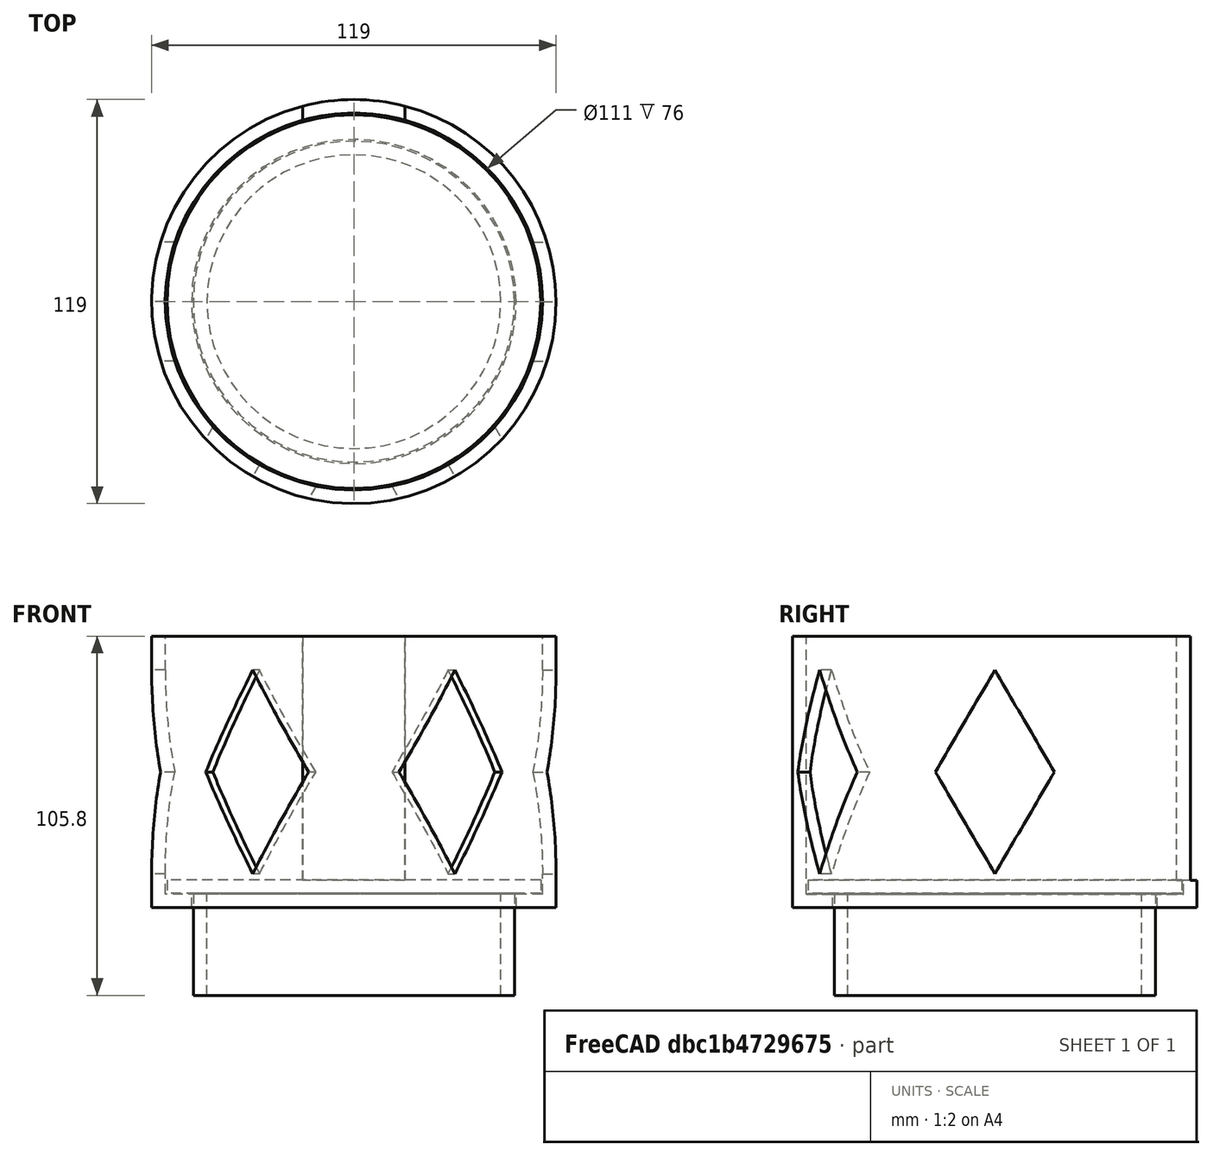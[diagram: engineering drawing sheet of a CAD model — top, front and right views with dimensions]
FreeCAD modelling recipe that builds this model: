
FCSTD DOCUMENT  (FreeCAD 0.19R14555 (Git shallow))
Label: mug_holder
License: All rights reserved
LicenseURL: http://en.wikipedia.org/wiki/All_rights_reserved
objects: Sketcher::SketchObject×4, PartDesign::Revolution×2, PartDesign::Body×2, PartDesign::Pocket×2, Mesh::Feature×2, PartDesign::PolarPattern×1
note: 15 computed .brp shape members not serialized (recipe doc carries the construction recipe); baked Part::Feature solids carry a one-line shape summary decoded from their .brp

FEATURE [Sketcher::SketchObject] Sketch004  label="BottomSketch"
  FullyConstrained = true
  MapMode = 5
  Placement = pos=(0,0,0) rot=(1,0,0;1.5708rad)
  Support = -> [XZ_Plane]
  sketch-geometry (8):
    g0: LineSegment StartX=0 StartY=30 StartZ=0 EndX=0 EndY=34 EndZ=0
    g1: LineSegment StartX=0 StartY=34 StartZ=0 EndX=55 EndY=34 EndZ=0
    g2: LineSegment StartX=55 StartY=34 StartZ=0 EndX=55 EndY=30 EndZ=0
    g3: LineSegment StartX=55 StartY=30 StartZ=0 EndX=47.25 EndY=30 EndZ=0
    g4: LineSegment StartX=47.25 StartY=30 StartZ=0 EndX=47.25 EndY=0 EndZ=0
    g5: LineSegment StartX=47.25 StartY=0 StartZ=0 EndX=43.25 EndY=0 EndZ=0
    g6: LineSegment StartX=43.25 StartY=0 StartZ=0 EndX=43.25 EndY=30 EndZ=0
    g7: LineSegment StartX=43.25 StartY=30 StartZ=0 EndX=0 EndY=30 EndZ=0
  constraints (24):
    c: Coincident(g0,g1)
    c: Coincident(g1,g2)
    c: Coincident(g2,g3)
    c: Coincident(g3,g4)
    c: Coincident(g4,g5)
    c: Coincident(g5,g6)
    c: Coincident(g6,g7)
    c: Coincident(g7,g0)
    c: Horizontal(g1)
    c: Horizontal(g7)
    c: Horizontal(g3)
    c: Horizontal(g5)
    c: Vertical(g0)
    c: Vertical(g2)
    c: Vertical(g4)
    c: Vertical(g6)
    c: DistanceX(g5,g4) = 4
    c: DistanceY(g2,g1) = 4
    c: DistanceX(g-1,g4) = 47.25  'ChairInsetOuterRadius'
    c: Equal(g0,g2)
    c: DistanceY(g4,g3) = 30  'ChairInsetHeight'
    c: PointOnObject(g5,g-1)
    c: PointOnObject(g0,g-2)
    c: DistanceX(g1,g1) = 55  'CupFaceOuterRadius'
FEATURE [PartDesign::Revolution] Revolution  label="BottomRevolution"
  Angle = 360
  Axis = (0,2e-16,1)
  Base = (0,0,0)
  Placement = pos=(0,0,0) rot=(1,0,0;1.5708rad)
  Profile = -> Sketch004
  ReferenceAxis = -> Sketch004 [V_Axis]
  Reversed = true
FEATURE [PartDesign::Body] Body  label="Bottom"
  Group = -> [Sketch004,Revolution]
  Origin = -> Origin
  Tip = -> Revolution
FEATURE [Sketcher::SketchObject] Sketch
  FullyConstrained = true
  MapMode = 5
  Placement = pos=(0,0,0) rot=(1,0,0;1.5708rad)
  Support = -> [XZ_Plane001]
  expr: Constraints[17] = <<BottomSketch>>.Constraints.ChairInsetHeight - 0.2mm
  expr: Constraints[13] = <<BottomSketch>>.Constraints.ChairInsetOuterRadius + 0.5mm
  expr: Constraints[12] = <<BottomSketch>>.Constraints.CupFaceOuterRadius + 0.5mm
  sketch-geometry (6):
    g0: LineSegment StartX=47.75 StartY=29.8 StartZ=0 EndX=55.5 EndY=29.8 EndZ=0
    g1: LineSegment StartX=55.5 StartY=29.8 StartZ=0 EndX=55.5 EndY=105.8 EndZ=0
    g2: LineSegment StartX=55.5 StartY=105.8 StartZ=0 EndX=59.5 EndY=105.8 EndZ=0
    g3: LineSegment StartX=59.5 StartY=105.8 StartZ=0 EndX=59.5 EndY=25.8 EndZ=0
    g4: LineSegment StartX=59.5 StartY=25.8 StartZ=0 EndX=47.75 EndY=25.8 EndZ=0
    g5: LineSegment StartX=47.75 StartY=25.8 StartZ=0 EndX=47.75 EndY=29.8 EndZ=0
  constraints (18):
    c: Horizontal(g0)
    c: Coincident(g0,g1)
    c: Vertical(g1)
    c: Coincident(g1,g2)
    c: Horizontal(g2)
    c: Coincident(g2,g3)
    c: Vertical(g3)
    c: Coincident(g3,g4)
    c: Horizontal(g4)
    c: Coincident(g4,g5)
    c: Coincident(g5,g0)
    c: Vertical(g5)
    c: DistanceX(g-1,g0) = 55.5
    c: DistanceX(g-1,g4) = 47.75
    c: DistanceX(g1,g2) = 4
    c: DistanceY(g4,g0) = 4
    c: DistanceY(g3,g3) = 80
    c: DistanceY(g-1,g0) = 29.8
FEATURE [PartDesign::Revolution] Revolution001
  Angle = 360
  Axis = (0,2e-16,1)
  Base = (0,0,0)
  Placement = pos=(0,0,0) rot=(1,0,0;1.5708rad)
  Profile = -> Sketch
  ReferenceAxis = -> Sketch [V_Axis]
FEATURE [Sketcher::SketchObject] Sketch005
  ExternalGeometry = -> [Revolution001]
  FullyConstrained = true
  MapMode = 5
  Placement = pos=(0,0,0) rot=(0.57735,0.57735,0.57735;2.0944rad)
  Support = -> [YZ_Plane001]
  sketch-geometry (9):
    g0: LineSegment StartX=2.91e-14 StartY=35.8 StartZ=0 EndX=-17.5 EndY=65.8 EndZ=0
    g1: LineSegment StartX=-17.5 StartY=65.8 StartZ=0 EndX=2.84e-14 EndY=95.8 EndZ=0
    g2: LineSegment StartX=2.91e-14 StartY=95.8 StartZ=0 EndX=17.5 EndY=65.8 EndZ=0
    g3: LineSegment StartX=17.5 StartY=65.8 StartZ=0 EndX=2.84e-14 EndY=35.8 EndZ=0
    g4: LineSegment StartX=2.91e-14 StartY=95.8 StartZ=0 EndX=2.91e-14 EndY=35.8 EndZ=0
    g5: LineSegment StartX=-17.5 StartY=65.8 StartZ=0 EndX=17.5 EndY=65.8 EndZ=0
    g6: LineSegment StartX=59.5 StartY=105.8 StartZ=0 EndX=-59.5 EndY=25.8 EndZ=0
    g7: GeomPoint X=2.85e-14 Y=65.8 Z=0
    g8: GeomPoint X=2.85e-14 Y=65.8 Z=0
  constraints (19):
    c: Coincident(g0,g1)
    c: Coincident(g1,g2)
    c: Coincident(g2,g3)
    c: Coincident(g3,g0)
    c: Coincident(g4,g1)
    c: Coincident(g4,g0)
    c: Vertical(g4)
    c: Coincident(g5,g0)
    c: Coincident(g5,g2)
    c: Horizontal(g5)
    c: Equal(g0,g1)
    c: Equal(g1,g2)
    c: Coincident(g6,g-4)
    c: Coincident(g6,g-3)
    c: Symmetric(g6,g6,g7)
    c: Symmetric(g0,g2,g8)
    c: Coincident(g7,g8)
    c: DistanceY(g0,g1) = 60
    c: DistanceX(g0,g2) = 35
FEATURE [PartDesign::Pocket] Pocket
  BaseFeature = -> Revolution001
  Length = 5
  Length2 = 100
  Placement = pos=(0,0,0) rot=(1,0,0;1.5708rad)
  Profile = -> Sketch005
  Type = 1
FEATURE [PartDesign::PolarPattern] PolarPattern
  Angle = 180
  Axis = -> Sketch005 [V_Axis]
  BaseFeature = -> Pocket
  Occurrences = 4
  Originals = -> [Pocket]
  Placement = pos=(0,0,0) rot=(1,0,0;1.5708rad)
FEATURE [Sketcher::SketchObject] Sketch006
  FullyConstrained = true
  MapMode = 5
  Placement = pos=(0,1.175e-13,105.8) rot=(0,0,1;3.14159rad)
  Support = -> [PolarPattern]
  sketch-geometry (4):
    g0: LineSegment StartX=-15 StartY=0 StartZ=0 EndX=15 EndY=0 EndZ=0
    g1: LineSegment StartX=15 StartY=0 StartZ=0 EndX=15 EndY=-75 EndZ=0
    g2: LineSegment StartX=15 StartY=-75 StartZ=0 EndX=-15 EndY=-75 EndZ=0
    g3: LineSegment StartX=-15 StartY=-75 StartZ=0 EndX=-15 EndY=0 EndZ=0
  constraints (11):
    c: Coincident(g0,g1)
    c: Coincident(g1,g2)
    c: Coincident(g2,g3)
    c: Coincident(g3,g0)
    c: Horizontal(g0)
    c: Horizontal(g2)
    c: Vertical(g1)
    c: Vertical(g3)
    c: Symmetric(g0,g0,g-1)
    c: DistanceY(g1,g1) = 75
    c: DistanceX(g0,g0) = 30
FEATURE [PartDesign::Pocket] Pocket001
  BaseFeature = -> PolarPattern
  Length = 72
  Length2 = 100
  Placement = pos=(0,0,0) rot=(1,0,0;1.5708rad)
  Profile = -> Sketch006
  Type = 0
FEATURE [PartDesign::Body] Body001  label="Top"
  Group = -> [Sketch,Revolution001,Sketch005,Pocket,PolarPattern,Sketch006,Pocket001]
  Origin = -> Origin001
  Tip = -> Pocket001
FEATURE [Mesh::Feature] Mesh  label="Top (Meshed)"
FEATURE [Mesh::Feature] Mesh001  label="Bottom (Meshed)"
